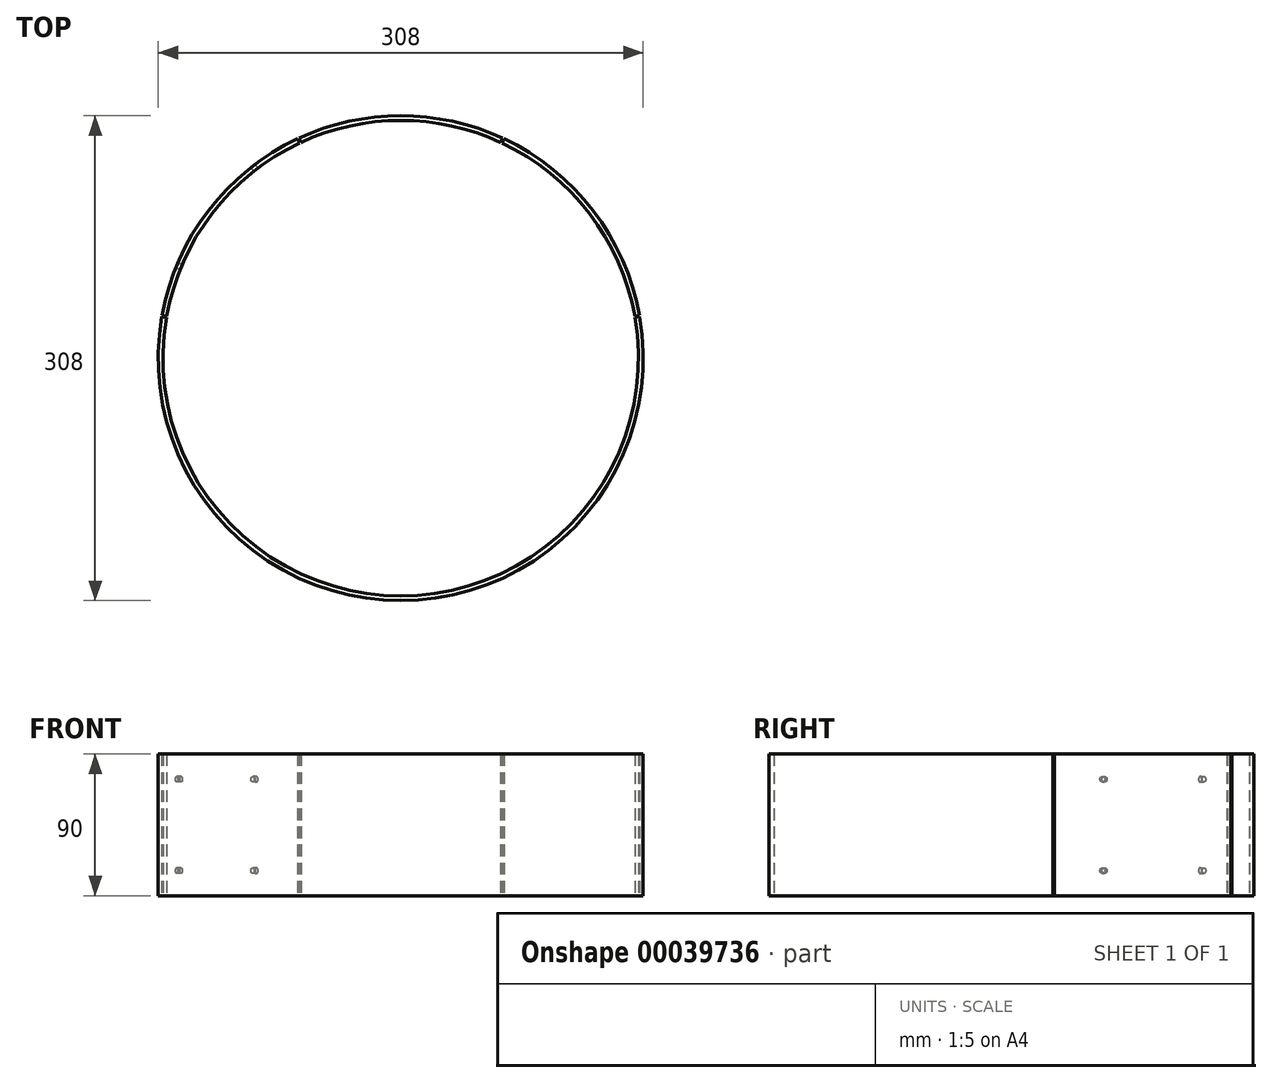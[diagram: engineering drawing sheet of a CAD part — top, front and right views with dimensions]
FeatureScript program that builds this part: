
annotation { "Feature Type Name" : "Feature", "Feature Type Description" : "" }
export const myFeature = defineFeature(function(context is Context, id is Id, definition is map)
    precondition{}
    {
        {
            var Q0;
            Q0=qCreatedBy(makeId("Top.planeOp"),FACE);
            var sketch = newSketch(context, id + "F0", { "sketchPlane" : qUnion([Q0])});
            skCircle(sketch, "E0", {"center": v(0, 0) * mm, "radius": 151 * mm});
            skCircle(sketch, "E1.0", {"center": v(0, 0) * mm, "radius": 154 * mm});
            skCircle(sketch, "E2.0", {"center": v(0, 0) * mm, "radius": 152.5 * mm, "construction": true});
            skLineSegment(sketch, "E3", {"start": v(0, 0) * mm, "end": v(0, 154) * mm, "construction": true});
            skLineSegment(sketch, "E4", {"start": v(0, 0) * mm, "end": v(65.08, 139.57) * mm, "construction": true});
            skLineSegment(sketch, "E5", {"start": v(0, 0) * mm, "end": v(-65.08, 139.57) * mm, "construction": true});
            skLineSegment(sketch, "E6", {"start": v(0, 0) * mm, "end": v(151.66, 26.74) * mm, "construction": true});
            skLineSegment(sketch, "E7", {"start": v(0, 0) * mm, "end": v(-151.66, 26.74) * mm, "construction": true});
            skLineSegment(sketch, "E8", {"start": v(-64.17, 136.68) * mm, "end": v(-64.81, 138.04) * mm});
            skLineSegment(sketch, "E9", {"start": v(-64.81, 138.04) * mm, "end": v(-65.45, 139.4) * mm});
            skLineSegment(sketch, "E10", {"start": v(-63.46, 137.02) * mm, "end": v(-64.09, 138.38) * mm});
            skLineSegment(sketch, "E11", {"start": v(-64.09, 138.38) * mm, "end": v(-64.72, 139.74) * mm});
            skPoint(sketch, "E12", {"position": v(-64.45, 138.21) * mm});
            skLineSegment(sketch, "E13.1.0", {"start": v(64.09, 138.38) * mm, "end": v(64.72, 139.74) * mm});
            skLineSegment(sketch, "E13.1.1", {"start": v(63.46, 137.02) * mm, "end": v(64.09, 138.38) * mm});
            skPoint(sketch, "E13.1.2", {"position": v(64.45, 138.21) * mm});
            skLineSegment(sketch, "E13.1.3", {"start": v(64.81, 138.04) * mm, "end": v(65.45, 139.4) * mm});
            skLineSegment(sketch, "E13.1.4", {"start": v(64.17, 136.68) * mm, "end": v(64.81, 138.04) * mm});
            skLineSegment(sketch, "E13.anchor1", {"start": v(0, 0) * mm, "end": v(-64.45, 138.21) * mm, "construction": true});
            skLineSegment(sketch, "E13.anchor2", {"start": v(0, 0) * mm, "end": v(64.45, 138.21) * mm, "construction": true});
            skLineSegment(sketch, "E14.1.0", {"start": v(-150.25, 26.09) * mm, "end": v(-151.73, 26.34) * mm});
            skLineSegment(sketch, "E14.1.1", {"start": v(-148.77, 25.83) * mm, "end": v(-150.25, 26.09) * mm});
            skLineSegment(sketch, "E14.1.2", {"start": v(-148.64, 26.61) * mm, "end": v(-150.11, 26.88) * mm});
            skLineSegment(sketch, "E14.1.3", {"start": v(-150.11, 26.88) * mm, "end": v(-151.59, 27.14) * mm});
            skPoint(sketch, "E14.1.4", {"position": v(-150.18, 26.48) * mm});
            skLineSegment(sketch, "E14.anchor2", {"start": v(0, 0) * mm, "end": v(-150.18, 26.48) * mm, "construction": true});
            skLineSegment(sketch, "E15.1.0", {"start": v(150.11, 26.88) * mm, "end": v(151.59, 27.14) * mm});
            skLineSegment(sketch, "E15.1.1", {"start": v(148.64, 26.61) * mm, "end": v(150.11, 26.88) * mm});
            skLineSegment(sketch, "E15.1.2", {"start": v(150.25, 26.09) * mm, "end": v(151.73, 26.34) * mm});
            skLineSegment(sketch, "E15.1.3", {"start": v(148.77, 25.83) * mm, "end": v(150.25, 26.09) * mm});
            skPoint(sketch, "E15.1.4", {"position": v(150.18, 26.48) * mm});
            skLineSegment(sketch, "E15.anchor2", {"start": v(0, 0) * mm, "end": v(150.18, 26.48) * mm, "construction": true});
            skLineSegment(sketch, "E16", {"start": v(-33.33, 150.35) * mm, "end": v(0, 0) * mm, "construction": true});
            skLineSegment(sketch, "E17", {"start": v(0, 0) * mm, "end": v(33.33, 150.35) * mm, "construction": true});
            skLineSegment(sketch, "E18", {"start": v(93.75, 122.18) * mm, "end": v(0, 0) * mm, "construction": true});
            skLineSegment(sketch, "E19", {"start": v(0, 0) * mm, "end": v(142.28, 58.93) * mm, "construction": true});
            skLineSegment(sketch, "E20", {"start": v(-93.75, 122.18) * mm, "end": v(0, 0) * mm, "construction": true});
            skLineSegment(sketch, "E21", {"start": v(0, 0) * mm, "end": v(-142.28, 58.93) * mm, "construction": true});
            skLineSegment(sketch, "E22", {"start": v(0, 0) * mm, "end": v(-150.63, 32.02) * mm, "construction": true});
            skLineSegment(sketch, "E23", {"start": v(0, 0) * mm, "end": v(-69.91, 137.22) * mm, "construction": true});
            skLineSegment(sketch, "E24", {"start": v(0, 0) * mm, "end": v(-60.17, 141.76) * mm, "construction": true});
            skLineSegment(sketch, "E25", {"start": v(0, 0) * mm, "end": v(60.17, 141.76) * mm, "construction": true});
            skArc(sketch, "E26", {"start": v(-59.59, 140.38) * mm, "mid": v(0, 152.5) * mm, "end": v(59.59, 140.38) * mm});
            skSolve(sketch);
        }
        {
            var Q0;
            {var subQ3=sQuery(id+"F0.wireOp",EDGE,"E8");Q0=makeQuery(id+"F0.imprint","IMPRINT",FACE,{"disambiguationData":[TD([[makeQuery(id+"F0.imprint","IMPRINT",EDGE,{"derivedFrom":subQ3}),1.0]])]});}
            var Q1;
            {var subQ3=sQuery(id+"F0.wireOp",EDGE,"E10");Q1=makeQuery(id+"F0.imprint","IMPRINT",FACE,{"disambiguationData":[TD([[makeQuery(id+"F0.imprint","IMPRINT",EDGE,{"derivedFrom":subQ3}),-1.0]])]});}
            var Q2;
            {var subQ5=sQuery(id+"F0.wireOp",EDGE,"E13.1.3");Q2=makeQuery(id+"F0.imprint","IMPRINT",FACE,{"disambiguationData":[TD([[makeQuery(id+"F0.imprint","IMPRINT",EDGE,{"derivedFrom":subQ5}),-1.0]])]});}
            var Q3;
            {var subQ2=sQuery(id+"F0.wireOp",EDGE,"E14.1.0");Q3=makeQuery(id+"F0.imprint","IMPRINT",FACE,{"disambiguationData":[TD([[makeQuery(id+"F0.imprint","IMPRINT",EDGE,{"derivedFrom":subQ2}),1.0]])]});}
            extrude(context, id + "F1", {"entities" : qUnion([Q0, Q1, Q2, Q3]), "depth" : 90 * mm});
        }
        {
            var Q0;
            Q0=sQuery(id+"F0.wireOp",EDGE,"E21");
            var Q1;
            Q1=sQuery(id+"F0.wireOp",VERTEX,"E21.end");
            cPlane(context, id + "F2", {"entities" : qUnion([Q0, Q1]), "cplaneType" : CPlaneType.LINE_POINT, "offset" : 150 * mm, "width" : 150 * mm, "height" : 150 * mm});
        }
        {
            var Q0;
            Q0=sQuery(id+"F0.wireOp",EDGE,"E20");
            var Q1;
            Q1=sQuery(id+"F0.wireOp",VERTEX,"E20.start");
            cPlane(context, id + "F3", {"entities" : qUnion([Q0, Q1]), "cplaneType" : CPlaneType.LINE_POINT, "offset" : 150 * mm, "width" : 150 * mm, "height" : 150 * mm});
        }
        {
            var Q0;
            Q0=qCreatedBy(id+"F2.planeOp",FACE);
            var sketch = newSketch(context, id + "F4", { "sketchPlane" : qUnion([Q0])});
            skLineSegment(sketch, "E27", {"start": v(0, 0) * mm, "end": v(0, 90) * mm, "construction": true});
            skLineSegment(sketch, "E28.0", {"start": v(-103.74, 90) * mm, "end": v(32.94, 90) * mm, "construction": true});
            skPoint(sketch, "E29", {"position": v(0, 16) * mm});
            skPoint(sketch, "E30", {"position": v(0, 74) * mm});
            skSolve(sketch);
        }
        {
            var Q0;
            Q0=sQuery(id+"F4.wireOp",VERTEX,"E29");
            var Q1;
            Q1=sQuery(id+"F4.wireOp",VERTEX,"E30");
            var Q2;
            Q2=makeQuery(id+"F1.opExtrude","SWEPT_BODY",BODY,{"disambiguationData":[OSD([sQuery(id+"F0.wireOp",EDGE,"E0"),sQuery(id+"F0.wireOp",EDGE,"E1.0"),sQuery(id+"F0.wireOp",EDGE,"E8"),sQuery(id+"F0.wireOp",EDGE,"E9"),sQuery(id+"F0.wireOp",EDGE,"E14.1.2"),sQuery(id+"F0.wireOp",EDGE,"E14.1.3")])]});
            hole(context, id + "F5", {"style" : HoleStyle.SIMPLE, "holeDiameter" : 3.5 * mm, "endStyle" : HoleEndStyle.THROUGH, "locations" : qUnion([Q0, Q1]), "scope" : qUnion([Q2])});
        }
        {
            var Q0;
            Q0=qCreatedBy(id+"F3.planeOp",FACE);
            var sketch = newSketch(context, id + "F6", { "sketchPlane" : qUnion([Q0])});
            skLineSegment(sketch, "E31.0", {"start": v(-103.74, 90) * mm, "end": v(32.94, 90) * mm, "construction": true});
            skLineSegment(sketch, "E32", {"start": v(0, 0) * mm, "end": v(0, 90) * mm, "construction": true});
            skPoint(sketch, "E33", {"position": v(0, 16) * mm});
            skPoint(sketch, "E34", {"position": v(0, 74) * mm});
            skCircle(sketch, "E35", {"center": v(0, 16) * mm, "radius": 1.75 * mm});
            skCircle(sketch, "E36", {"center": v(0, 74) * mm, "radius": 1.75 * mm});
            skSolve(sketch);
        }
        {
            var Q0;
            Q0 = qSketchRegion(id + "F6", true);
            extrude(context, id + "F7", {"entities" : qUnion([Q0]), "operationType" : NewBodyOperationType.REMOVE, "endBound" : BoundingType.UP_TO_NEXT, "depth" : 25 * mm});
        }
    });
